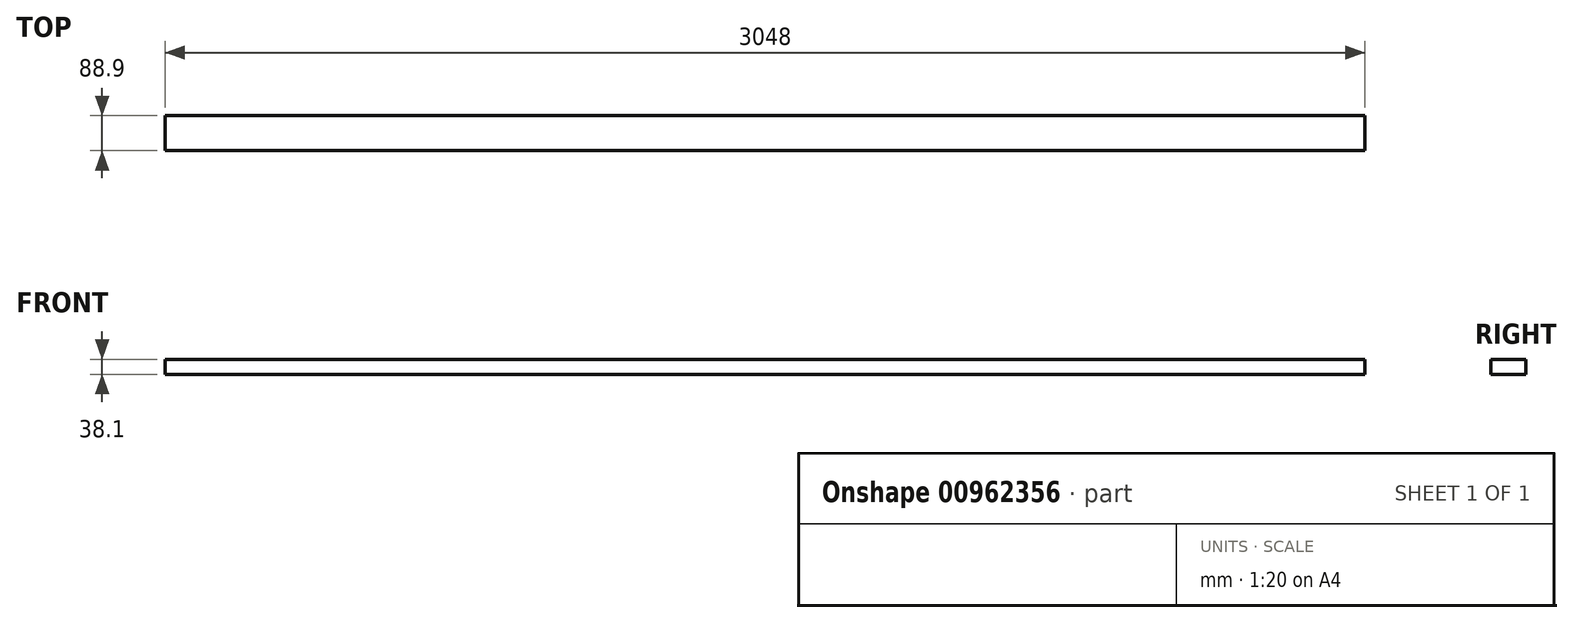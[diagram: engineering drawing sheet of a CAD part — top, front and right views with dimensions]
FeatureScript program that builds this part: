
annotation { "Feature Type Name" : "Feature", "Feature Type Description" : "" }
export const myFeature = defineFeature(function(context is Context, id is Id, definition is map)
    precondition{}
    {
        {
            var Q0;
            Q0=qCreatedBy(makeId("Right.planeOp"),FACE);
            var sketch = newSketch(context, id + "F0", { "sketchPlane" : qUnion([Q0])});
            skLineSegment(sketch, "E0.bottom", {"start": v(44.45, -19.05) * mm, "end": v(-44.45, -19.05) * mm});
            skLineSegment(sketch, "E0.top", {"start": v(44.45, 19.05) * mm, "end": v(-44.45, 19.05) * mm});
            skLineSegment(sketch, "E0.left", {"start": v(44.45, -19.05) * mm, "end": v(44.45, 19.05) * mm});
            skLineSegment(sketch, "E0.right", {"start": v(-44.45, -19.05) * mm, "end": v(-44.45, 19.05) * mm});
            skPoint(sketch, "E0.middle", {"position": v(0, 0) * mm});
            skSolve(sketch);
        }
        {
            var Q0;
            Q0=qSketchRegion(id+"F0",true);
            var Q1;
            Q1=makeQuery(id+"F0.imprint","IMPRINT",FACE,{"disambiguationData":[TD([[makeQuery(id+"F0.imprint","IMPRINT",EDGE,{"derivedFrom":sQuery(id+"F0.wireOp",EDGE,"E0.bottom")}),-1.0]])]});
            extrude(context, id + "F1", {"entities" : qUnion([Q0, Q1]), "depth" : 3048 * mm, "offsetDistance" : 25.4 * mm});
        }
    });
